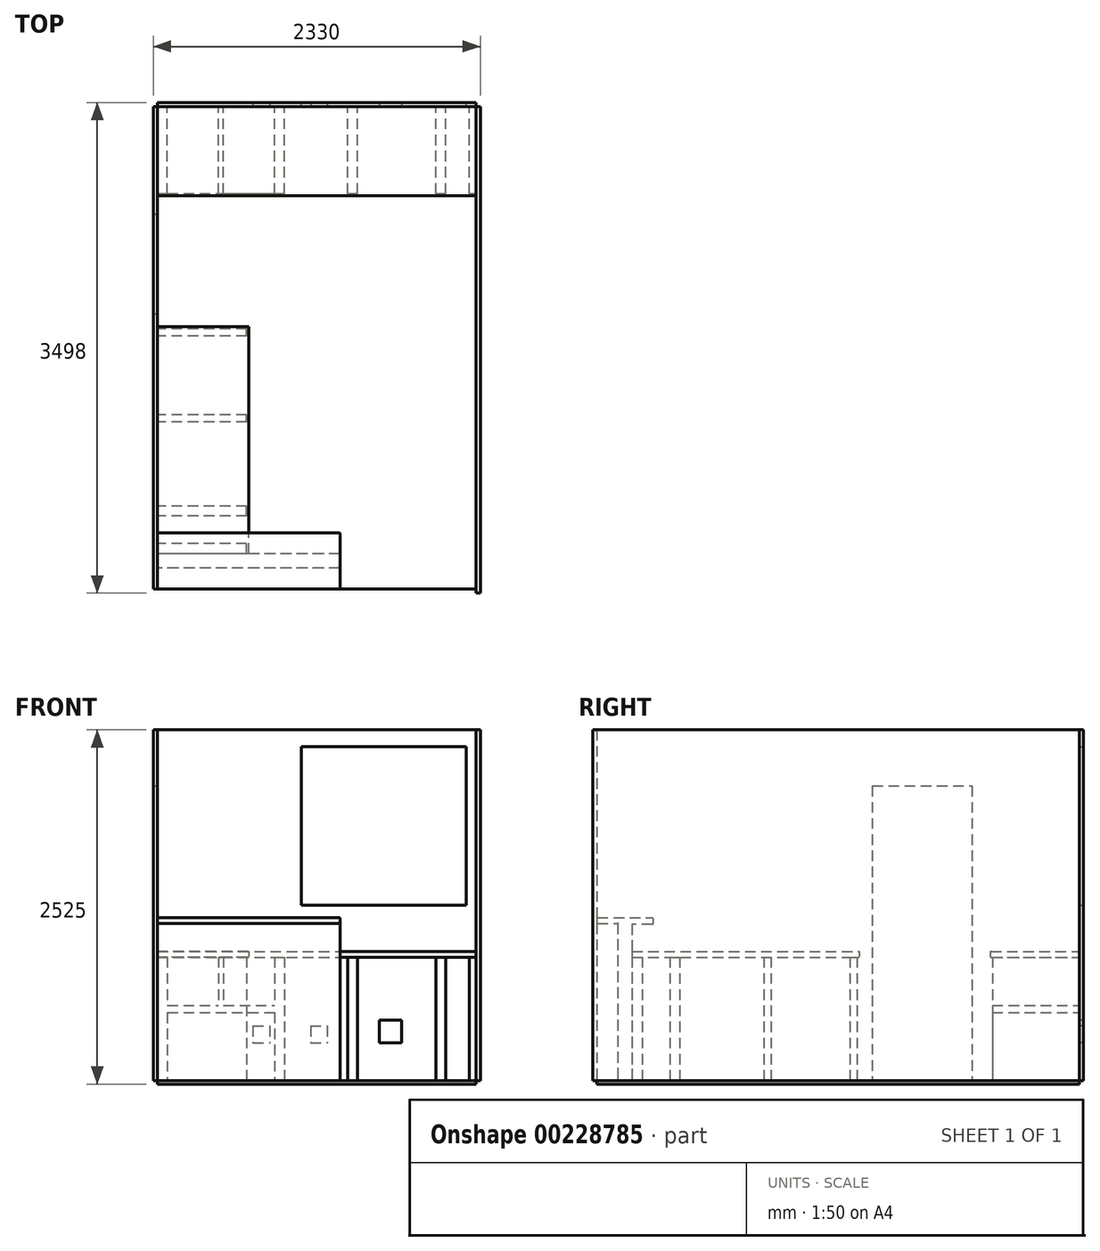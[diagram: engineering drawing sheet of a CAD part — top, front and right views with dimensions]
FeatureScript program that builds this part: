
annotation { "Feature Type Name" : "Feature", "Feature Type Description" : "" }
export const myFeature = defineFeature(function(context is Context, id is Id, definition is map)
    precondition{}
    {
        {
            var Q0;
            Q0=qCreatedBy(makeId("Top.planeOp"),FACE);
            var sketch = newSketch(context, id + "F0", { "sketchPlane" : qUnion([Q0])});
            skLineSegment(sketch, "E0.bottom", {"start": v(-166.7, 1726.55) * mm, "end": v(-136.7, 1726.55) * mm});
            skLineSegment(sketch, "E0.top", {"start": v(-166.7, -1711.45) * mm, "end": v(-136.7, -1711.45) * mm});
            skLineSegment(sketch, "E0.left", {"start": v(-166.7, 1726.55) * mm, "end": v(-166.7, -1711.45) * mm});
            skLineSegment(sketch, "E0.right", {"start": v(-136.7, 1726.55) * mm, "end": v(-136.7, -1711.45) * mm});
            skLineSegment(sketch, "E1.bottom", {"start": v(-136.7, 1756.55) * mm, "end": v(2133.3, 1756.55) * mm});
            skLineSegment(sketch, "E1.top", {"start": v(-136.7, 1726.55) * mm, "end": v(2133.3, 1726.55) * mm});
            skLineSegment(sketch, "E1.left", {"start": v(-136.7, 1756.55) * mm, "end": v(-136.7, 1726.55) * mm});
            skLineSegment(sketch, "E1.right", {"start": v(2133.3, 1756.55) * mm, "end": v(2133.3, 1726.55) * mm});
            skLineSegment(sketch, "E2.bottom", {"start": v(2133.3, 1726.55) * mm, "end": v(2163.3, 1726.55) * mm});
            skLineSegment(sketch, "E2.top", {"start": v(2133.3, -1741.45) * mm, "end": v(2163.3, -1741.45) * mm});
            skLineSegment(sketch, "E2.left", {"start": v(2133.3, 1726.55) * mm, "end": v(2133.3, -1741.45) * mm});
            skLineSegment(sketch, "E2.right", {"start": v(2163.3, 1726.55) * mm, "end": v(2163.3, -1741.45) * mm});
            skLineSegment(sketch, "E3.bottom", {"start": v(-166.7, 961.55) * mm, "end": v(-136.7, 961.55) * mm});
            skLineSegment(sketch, "E3.top", {"start": v(-166.7, 251.55) * mm, "end": v(-136.7, 251.55) * mm});
            skLineSegment(sketch, "E3.left", {"start": v(-166.7, 961.55) * mm, "end": v(-166.7, 251.55) * mm});
            skLineSegment(sketch, "E3.right", {"start": v(-136.7, 961.55) * mm, "end": v(-136.7, 251.55) * mm});
            skSolve(sketch);
        }
        {
            var Q0;
            Q0=makeQuery(id+"F0.imprint","IMPRINT",FACE,{"disambiguationData":[TD([[makeQuery(id+"F0.imprint","IMPRINT",EDGE,{"derivedFrom":sQuery(id+"F0.wireOp",EDGE,"E1.bottom")}),-1.0]])]});
            var Q1;
            Q1=makeQuery(id+"F0.imprint","IMPRINT",FACE,{"disambiguationData":[TD([[makeQuery(id+"F0.imprint","IMPRINT",EDGE,{"derivedFrom":sQuery(id+"F0.wireOp",EDGE,"E2.bottom")}),-1.0]])]});
            var Q2;
            {var subQ0=sQuery(id+"F0.wireOp",EDGE,"E0.bottom");Q2=makeQuery(id+"F0.imprint","IMPRINT",FACE,{"disambiguationData":[TD([[makeQuery(id+"F0.imprint","IMPRINT",EDGE,{"derivedFrom":subQ0}),-1.0]])]});}
            var Q3;
            {var subQ0=sQuery(id+"F0.wireOp",EDGE,"E0.top");Q3=makeQuery(id+"F0.imprint","IMPRINT",FACE,{"disambiguationData":[TD([[makeQuery(id+"F0.imprint","IMPRINT",EDGE,{"derivedFrom":subQ0}),1.0]])]});}
            extrude(context, id + "F1", {"entities" : qUnion([Q0, Q1, Q2, Q3]), "depth" : 2500 * mm});
        }
        {
            var Q0;
            Q0=makeQuery(id+"F1.opExtrude","CAP_FACE",FACE,{"disambiguationData":[OSD([sQuery(id+"F0.wireOp",EDGE,"E0.top"),sQuery(id+"F0.wireOp",EDGE,"E0.left"),sQuery(id+"F0.wireOp",EDGE,"E0.right"),sQuery(id+"F0.wireOp",EDGE,"E3.top")])],"isStart":true});
            var sketch = newSketch(context, id + "F2", { "sketchPlane" : qUnion([Q0])});
            skLineSegment(sketch, "E4.bottom", {"start": v(-136.7, 1711.45) * mm, "end": v(2133.3, 1711.45) * mm});
            skLineSegment(sketch, "E4.top", {"start": v(-136.7, -1726.55) * mm, "end": v(2133.3, -1726.55) * mm});
            skLineSegment(sketch, "E4.left", {"start": v(-136.7, 1711.45) * mm, "end": v(-136.7, -1726.55) * mm});
            skLineSegment(sketch, "E4.right", {"start": v(2133.3, 1711.45) * mm, "end": v(2133.3, -1726.55) * mm});
            skSolve(sketch);
        }
        {
            var Q0;
            Q0 = qSketchRegion(id + "F2", true);
            extrude(context, id + "F3", {"entities" : qUnion([Q0]), "depth" : 25 * mm});
        }
        {
            var Q0;
            Q0=makeQuery(id+"F1.opExtrude","SWEPT_FACE",FACE,{"disambiguationData":[OSD([sQuery(id+"F0.wireOp",EDGE,"E1.top")])]});
            var sketch = newSketch(context, id + "F4", { "sketchPlane" : qUnion([Q0])});
            skLineSegment(sketch, "E5.bottom", {"start": v(-136.7, 2500) * mm, "end": v(2133.3, 2500) * mm, "construction": true});
            skLineSegment(sketch, "E5.top", {"start": v(-136.7, 0) * mm, "end": v(2133.3, 0) * mm, "construction": true});
            skLineSegment(sketch, "E5.left", {"start": v(-136.7, 2500) * mm, "end": v(-136.7, 0) * mm, "construction": true});
            skLineSegment(sketch, "E5.right", {"start": v(2133.3, 2500) * mm, "end": v(2133.3, 0) * mm, "construction": true});
            skLineSegment(sketch, "E6", {"start": v(-136.7, 920) * mm, "end": v(2133.3, 920) * mm, "construction": true});
            skLineSegment(sketch, "E7.bottom", {"start": v(-136.7, 920) * mm, "end": v(2133.3, 920) * mm});
            skLineSegment(sketch, "E7.top", {"start": v(-136.7, 880) * mm, "end": v(2133.3, 880) * mm});
            skLineSegment(sketch, "E7.left", {"start": v(-136.7, 920) * mm, "end": v(-136.7, 880) * mm});
            skLineSegment(sketch, "E7.right", {"start": v(2133.3, 920) * mm, "end": v(2133.3, 880) * mm});
            skLineSegment(sketch, "E8.bottom", {"start": v(543.3, 390) * mm, "end": v(663.3, 390) * mm});
            skLineSegment(sketch, "E8.top", {"start": v(543.3, 270) * mm, "end": v(663.3, 270) * mm});
            skLineSegment(sketch, "E8.left", {"start": v(543.3, 390) * mm, "end": v(543.3, 270) * mm});
            skLineSegment(sketch, "E8.right", {"start": v(663.3, 390) * mm, "end": v(663.3, 270) * mm});
            skLineSegment(sketch, "E9.bottom", {"start": v(953.3, 390) * mm, "end": v(1073.3, 390) * mm});
            skLineSegment(sketch, "E9.top", {"start": v(953.3, 270) * mm, "end": v(1073.3, 270) * mm});
            skLineSegment(sketch, "E9.left", {"start": v(953.3, 390) * mm, "end": v(953.3, 270) * mm});
            skLineSegment(sketch, "E9.right", {"start": v(1073.3, 390) * mm, "end": v(1073.3, 270) * mm});
            skLineSegment(sketch, "E10.bottom", {"start": v(1443.3, 430) * mm, "end": v(1603.3, 430) * mm});
            skLineSegment(sketch, "E10.top", {"start": v(1443.3, 270) * mm, "end": v(1603.3, 270) * mm});
            skLineSegment(sketch, "E10.left", {"start": v(1443.3, 430) * mm, "end": v(1443.3, 270) * mm});
            skLineSegment(sketch, "E10.right", {"start": v(1603.3, 430) * mm, "end": v(1603.3, 270) * mm});
            skSolve(sketch);
        }
        {
            var Q0;
            Q0=makeQuery(id+"F4.imprint","IMPRINT",FACE,{"disambiguationData":[TD([[makeQuery(id+"F4.imprint","IMPRINT",EDGE,{"derivedFrom":sQuery(id+"F4.wireOp",EDGE,"E7.bottom")}),-1.0]])]});
            extrude(context, id + "F5", {"entities" : qUnion([Q0]), "depth" : 635 * mm});
        }
        {
            var Q0;
            {var subQ0=sQuery(id+"F0.wireOp",EDGE,"E0.right");Q0=makeQuery(id+"F1.opExtrude","SWEPT_FACE",FACE,{"disambiguationData":[OSD([subQ0]),TDD([makeQuery(id+"F0.imprint","IMPRINT",EDGE,{"disambiguationData":[TD([[makeQuery(id+"F0.imprint","INTERSECT",VERTEX,{"derivedFrom":[sQuery(id+"F0.wireOp",EDGE,"E0.top"),subQ0]}),1.0]])],"derivedFrom":subQ0})])]});}
            var sketch = newSketch(context, id + "F6", { "sketchPlane" : qUnion([Q0])});
            skLineSegment(sketch, "E11.top", {"start": v(-1461.45, 880) * mm, "end": v(159.45, 880) * mm});
            skLineSegment(sketch, "E11.left", {"start": v(-1461.45, 920) * mm, "end": v(-1461.45, 880) * mm});
            skLineSegment(sketch, "E11.right", {"start": v(159.45, 920) * mm, "end": v(159.45, 880) * mm});
            skLineSegment(sketch, "E12", {"start": v(-1511.45, 1160) * mm, "end": v(-1711.45, 1160) * mm});
            skLineSegment(sketch, "E13", {"start": v(-1711.45, 1120) * mm, "end": v(-1561.45, 1120) * mm});
            skLineSegment(sketch, "E14", {"start": v(-1561.45, 1120) * mm, "end": v(-1561.45, 0) * mm});
            skLineSegment(sketch, "E15.MirrorCS", {"start": v(-1311.45, 1113.32) * mm, "end": v(-1460.49, 1113.32) * mm});
            skLineSegment(sketch, "E16.MirrorCS", {"start": v(-1511.45, 1160) * mm, "end": v(-1311.45, 1160) * mm});
            skLineSegment(sketch, "E17", {"start": v(-1711.45, 1160) * mm, "end": v(-1711.45, 1120) * mm});
            skLineSegment(sketch, "E18", {"start": v(-1311.45, 1160) * mm, "end": v(-1311.45, 1113.32) * mm});
            skLineSegment(sketch, "E19", {"start": v(-1561.45, 0) * mm, "end": v(-1461.45, 0) * mm});
            skLineSegment(sketch, "E20", {"start": v(-1460.55, 920) * mm, "end": v(-1460.55, 880) * mm});
            skLineSegment(sketch, "E21", {"start": v(-1460.55, 920) * mm, "end": v(159.45, 920) * mm});
            skLineSegment(sketch, "E22", {"start": v(-1460.49, 1113.32) * mm, "end": v(-1461.45, 0) * mm});
            skSolve(sketch);
        }
        {
            var Q0;
            Q0=makeQuery(id+"F6.imprint","IMPRINT",FACE,{"disambiguationData":[TD([[makeQuery(id+"F6.imprint","IMPRINT",EDGE,{"derivedFrom":sQuery(id+"F6.wireOp",EDGE,"E12")}),1.0]])]});
            extrude(context, id + "F7", {"entities" : qUnion([Q0]), "depth" : 1300 * mm});
        }
        {
            var Q0;
            {var subQ0=sQuery(id+"F6.wireOp",EDGE,"E11.right");Q0=makeQuery(id+"F6.imprint","IMPRINT",FACE,{"disambiguationData":[TD([[makeQuery(id+"F6.imprint","IMPRINT",EDGE,{"derivedFrom":subQ0}),-1.0]])]});}
            extrude(context, id + "F8", {"entities" : qUnion([Q0]), "operationType" : NewBodyOperationType.ADD, "depth" : 650 * mm});
        }
        {
            var Q0;
            Q0=makeQuery(id+"F1.opExtrude","SWEPT_FACE",FACE,{"disambiguationData":[OSD([sQuery(id+"F0.wireOp",EDGE,"E1.bottom")])]});
            var sketch = newSketch(context, id + "F9", { "sketchPlane" : qUnion([Q0])});
            skLineSegment(sketch, "E23.bottom", {"start": v(-886.3, 2380) * mm, "end": v(-2063.3, 2380) * mm});
            skLineSegment(sketch, "E23.top", {"start": v(-886.3, 1250) * mm, "end": v(-2063.3, 1250) * mm});
            skLineSegment(sketch, "E23.left", {"start": v(-886.3, 2380) * mm, "end": v(-886.3, 1250) * mm});
            skLineSegment(sketch, "E23.right", {"start": v(-2063.3, 2380) * mm, "end": v(-2063.3, 1250) * mm});
            skSolve(sketch);
        }
        {
            var Q0;
            Q0=makeQuery(id+"F9.imprint","IMPRINT",FACE,{"disambiguationData":[TD([[makeQuery(id+"F9.imprint","IMPRINT",EDGE,{"derivedFrom":sQuery(id+"F9.wireOp",EDGE,"E23.bottom")}),1.0]])]});
            extrude(context, id + "F10", {"entities" : qUnion([Q0]), "operationType" : NewBodyOperationType.REMOVE, "endBound" : BoundingType.THROUGH_ALL, "oppositeDirection" : true, "depth" : 25 * mm});
        }
        {
            var Q0;
            Q0=makeQuery(id+"F1.opExtrude","SWEPT_FACE",FACE,{"disambiguationData":[OSD([sQuery(id+"F0.wireOp",EDGE,"E3.bottom")])]});
            var sketch = newSketch(context, id + "F11", { "sketchPlane" : qUnion([Q0])});
            skLineSegment(sketch, "E24.bottom", {"start": v(-166.7, 2500) * mm, "end": v(-136.7, 2500) * mm});
            skLineSegment(sketch, "E24.top", {"start": v(-166.7, 2100) * mm, "end": v(-136.7, 2100) * mm});
            skLineSegment(sketch, "E24.left", {"start": v(-166.7, 2500) * mm, "end": v(-166.7, 2100) * mm});
            skLineSegment(sketch, "E24.right", {"start": v(-136.7, 2500) * mm, "end": v(-136.7, 2100) * mm});
            skSolve(sketch);
        }
        {
            var Q0;
            Q0=makeQuery(id+"F11.imprint","IMPRINT",FACE,{"disambiguationData":[TD([[makeQuery(id+"F11.imprint","IMPRINT",EDGE,{"derivedFrom":sQuery(id+"F11.wireOp",EDGE,"E24.bottom")}),-1.0]])]});
            extrude(context, id + "F12", {"entities" : qUnion([Q0]), "operationType" : NewBodyOperationType.ADD, "depth" : 710 * mm});
        }
        {
            var Q0;
            {var subQ0=sQuery(id+"F0.wireOp",EDGE,"E0.right");Q0=makeQuery(id+"F1.opExtrude","SWEPT_FACE",FACE,{"disambiguationData":[OSD([subQ0]),TDD([makeQuery(id+"F0.imprint","IMPRINT",EDGE,{"disambiguationData":[TD([[makeQuery(id+"F0.imprint","INTERSECT",VERTEX,{"derivedFrom":[sQuery(id+"F0.wireOp",EDGE,"E0.top"),subQ0]}),1.0]])],"derivedFrom":subQ0})])]});}
            var sketch = newSketch(context, id + "F13", { "sketchPlane" : qUnion([Q0])});
            skLineSegment(sketch, "E25", {"start": v(-1997.96, 880) * mm, "end": v(384.41, 880) * mm, "construction": true});
            skLineSegment(sketch, "E26", {"start": v(-1121.45, 0) * mm, "end": v(-1121.45, -0.15) * mm, "construction": true});
            skLineSegment(sketch, "E27.bottom", {"start": v(-1121.45, 880) * mm, "end": v(-1191.45, 880) * mm});
            skLineSegment(sketch, "E27.top", {"start": v(-1121.45, 0) * mm, "end": v(-1191.45, 0) * mm});
            skLineSegment(sketch, "E27.left", {"start": v(-1121.45, 880) * mm, "end": v(-1121.45, 0) * mm});
            skLineSegment(sketch, "E27.right", {"start": v(-1191.45, 880) * mm, "end": v(-1191.45, 0) * mm});
            skLineSegment(sketch, "E28.bottom", {"start": v(-1387.45, 880) * mm, "end": v(-1191.45, 880) * mm});
            skLineSegment(sketch, "E28.top", {"start": v(-1387.45, 0) * mm, "end": v(-1191.45, 0) * mm});
            skLineSegment(sketch, "E28.left", {"start": v(-1387.45, 880) * mm, "end": v(-1387.45, 0) * mm});
            skLineSegment(sketch, "E29.bottom", {"start": v(-1387.45, 880) * mm, "end": v(-1460.55, 880) * mm});
            skLineSegment(sketch, "E29.top", {"start": v(-1387.45, 0) * mm, "end": v(-1460.55, 0) * mm});
            skLineSegment(sketch, "E29.right", {"start": v(-1460.55, 880) * mm, "end": v(-1460.55, 0) * mm});
            skLineSegment(sketch, "E30.bottom", {"start": v(-1121.45, 880) * mm, "end": v(-521.45, 880) * mm});
            skLineSegment(sketch, "E30.top", {"start": v(-1121.45, 0) * mm, "end": v(-521.45, 0) * mm});
            skLineSegment(sketch, "E30.right", {"start": v(-521.45, 880) * mm, "end": v(-521.45, 0) * mm});
            skLineSegment(sketch, "E31.bottom", {"start": v(-521.45, 880) * mm, "end": v(-471.45, 880) * mm});
            skLineSegment(sketch, "E31.top", {"start": v(-521.45, 0) * mm, "end": v(-471.45, 0) * mm});
            skLineSegment(sketch, "E31.right", {"start": v(-471.45, 880) * mm, "end": v(-471.45, 0) * mm});
            skLineSegment(sketch, "E32.bottom", {"start": v(-471.45, 880) * mm, "end": v(92.55, 880) * mm});
            skLineSegment(sketch, "E32.top", {"start": v(-471.45, 0) * mm, "end": v(92.55, 0) * mm});
            skLineSegment(sketch, "E32.right", {"start": v(92.55, 880) * mm, "end": v(92.55, 0) * mm});
            skLineSegment(sketch, "E33.bottom", {"start": v(92.55, 880) * mm, "end": v(142.55, 880) * mm});
            skLineSegment(sketch, "E33.top", {"start": v(92.55, 0) * mm, "end": v(142.55, 0) * mm});
            skLineSegment(sketch, "E33.right", {"start": v(142.55, 880) * mm, "end": v(142.55, 0) * mm});
            skLineSegment(sketch, "E34", {"start": v(-821.45, 2500) * mm, "end": v(-821.45, 0) * mm, "construction": true});
            skSolve(sketch);
        }
        {
            var Q0;
            Q0=makeQuery(id+"F13.imprint","IMPRINT",FACE,{"disambiguationData":[TD([[makeQuery(id+"F13.imprint","IMPRINT",EDGE,{"derivedFrom":sQuery(id+"F13.wireOp",EDGE,"E27.bottom")}),-1.0]])]});
            var Q1;
            Q1=makeQuery(id+"F13.imprint","IMPRINT",FACE,{"disambiguationData":[TD([[makeQuery(id+"F13.imprint","IMPRINT",EDGE,{"derivedFrom":sQuery(id+"F13.wireOp",EDGE,"E29.bottom")}),-1.0]])]});
            var Q2;
            Q2=makeQuery(id+"F13.imprint","IMPRINT",FACE,{"disambiguationData":[TD([[makeQuery(id+"F13.imprint","IMPRINT",EDGE,{"derivedFrom":sQuery(id+"F13.wireOp",EDGE,"E31.bottom")}),-1.0]])]});
            var Q3;
            Q3=makeQuery(id+"F13.imprint","IMPRINT",FACE,{"disambiguationData":[TD([[makeQuery(id+"F13.imprint","IMPRINT",EDGE,{"derivedFrom":sQuery(id+"F13.wireOp",EDGE,"E33.bottom")}),-1.0]])]});
            extrude(context, id + "F14", {"entities" : qUnion([Q0, Q1, Q2, Q3]), "depth" : 635 * mm});
        }
        {
            var Q0;
            Q0=makeQuery(id+"F8.opExtrude","SWEPT_EDGE",EDGE,{"disambiguationData":[OSD([sQuery(id+"F6.wireOp",EDGE,"E11.right"),sQuery(id+"F6.wireOp",EDGE,"E21")])]});
            var Q1;
            Q1=makeQuery(id+"F8.opExtrude","CAP_EDGE",EDGE,{"disambiguationData":[OSD([sQuery(id+"F6.wireOp",EDGE,"E21")])],"isStart":false});
            var Q2;
            Q2=makeQuery(id+"F8.opExtrude","SWEPT_EDGE",EDGE,{"disambiguationData":[OSD([sQuery(id+"F6.wireOp",EDGE,"E11.top"),sQuery(id+"F6.wireOp",EDGE,"E11.right")])]});
            var Q3;
            Q3=makeQuery(id+"F8.opExtrude","CAP_EDGE",EDGE,{"disambiguationData":[OSD([sQuery(id+"F6.wireOp",EDGE,"E11.top")])],"isStart":false});
            fillet(context, id + "F15", {"entities" : qUnion([Q0, Q1, Q2, Q3]), "radius" : 5 * mm, "tangentPropagation" : true, "allowEdgeOverflow" : false});
        }
        {
            var Q0;
            Q0=makeQuery(id+"F7.opExtrude","SWEPT_EDGE",EDGE,{"disambiguationData":[OSD([sQuery(id+"F0.wireOp",EDGE,"E0.top"),sQuery(id+"F0.wireOp",EDGE,"E0.right"),sQuery(id+"F6.wireOp",EDGE,"E12"),sQuery(id+"F6.wireOp",EDGE,"E17")])]});
            var Q1;
            Q1=makeQuery(id+"F7.opExtrude","SWEPT_EDGE",EDGE,{"disambiguationData":[OSD([sQuery(id+"F6.wireOp",EDGE,"E16.MirrorCS"),sQuery(id+"F6.wireOp",EDGE,"E18")])]});
            var Q2;
            Q2=makeQuery(id+"F7.opExtrude","CAP_EDGE",EDGE,{"disambiguationData":[OSD([sQuery(id+"F6.wireOp",EDGE,"E12"),sQuery(id+"F6.wireOp",EDGE,"E16.MirrorCS")])],"isStart":false});
            var Q3;
            Q3=makeQuery(id+"F7.opExtrude","SWEPT_EDGE",EDGE,{"disambiguationData":[OSD([sQuery(id+"F0.wireOp",EDGE,"E0.top"),sQuery(id+"F0.wireOp",EDGE,"E0.right"),sQuery(id+"F6.wireOp",EDGE,"E13"),sQuery(id+"F6.wireOp",EDGE,"E17")])]});
            var Q4;
            Q4=makeQuery(id+"F7.opExtrude","CAP_EDGE",EDGE,{"disambiguationData":[OSD([sQuery(id+"F6.wireOp",EDGE,"E13")])],"isStart":false});
            var Q5;
            Q5=makeQuery(id+"F7.opExtrude","CAP_EDGE",EDGE,{"disambiguationData":[OSD([sQuery(id+"F6.wireOp",EDGE,"E15.MirrorCS")])],"isStart":false});
            var Q6;
            Q6=makeQuery(id+"F7.opExtrude","CAP_EDGE",EDGE,{"disambiguationData":[OSD([sQuery(id+"F6.wireOp",EDGE,"E17")])],"isStart":false});
            var Q7;
            Q7=makeQuery(id+"F7.opExtrude","CAP_EDGE",EDGE,{"disambiguationData":[OSD([sQuery(id+"F6.wireOp",EDGE,"E18")])],"isStart":false});
            var Q8;
            Q8=makeQuery(id+"F7.opExtrude","SWEPT_EDGE",EDGE,{"disambiguationData":[OSD([sQuery(id+"F6.wireOp",EDGE,"E15.MirrorCS"),sQuery(id+"F6.wireOp",EDGE,"E18")])]});
            fillet(context, id + "F16", {"entities" : qUnion([Q0, Q1, Q2, Q3, Q4, Q5, Q6, Q7, Q8]), "radius" : 5 * mm, "tangentPropagation" : true, "allowEdgeOverflow" : false});
        }
        {
            var Q0;
            Q0=makeQuery(id+"F5.opExtrude","CAP_EDGE",EDGE,{"disambiguationData":[OSD([sQuery(id+"F4.wireOp",EDGE,"E7.bottom")])],"isStart":false});
            var Q1;
            Q1=makeQuery(id+"F5.opExtrude","CAP_EDGE",EDGE,{"disambiguationData":[OSD([sQuery(id+"F4.wireOp",EDGE,"E7.top")])],"isStart":false});
            fillet(context, id + "F17", {"entities" : qUnion([Q0, Q1]), "radius" : 5 * mm, "tangentPropagation" : true, "allowEdgeOverflow" : false});
        }
        {
            var Q0;
            {var subQ0=sQuery(id+"F4.wireOp",EDGE,"E7.top");Q0=makeQuery(id+"F4.imprint","IMPRINT",FACE,{"disambiguationData":[TD([[makeQuery(id+"F4.imprint","IMPRINT",EDGE,{"derivedFrom":subQ0}),-1.0]])]});}
            var sketch = newSketch(context, id + "F18", { "sketchPlane" : qUnion([Q0])});
            skLineSegment(sketch, "E35", {"start": v(-136.7, 0) * mm, "end": v(-136.7, 880) * mm, "construction": true});
            skLineSegment(sketch, "E36", {"start": v(2133.3, 0) * mm, "end": v(2133.3, 880) * mm, "construction": true});
            skLineSegment(sketch, "E37", {"start": v(-136.7, 880) * mm, "end": v(2133.3, 880) * mm, "construction": true});
            skLineSegment(sketch, "E38.bottom", {"start": v(2133.3, 880) * mm, "end": v(2083.3, 880) * mm});
            skLineSegment(sketch, "E38.top", {"start": v(2133.3, 0) * mm, "end": v(2083.3, 0) * mm});
            skLineSegment(sketch, "E38.left", {"start": v(2133.3, 880) * mm, "end": v(2133.3, 0) * mm});
            skLineSegment(sketch, "E38.right", {"start": v(2083.3, 880) * mm, "end": v(2083.3, 0) * mm});
            skLineSegment(sketch, "E39.bottom", {"start": v(1287.3, 880) * mm, "end": v(1217.3, 880) * mm});
            skLineSegment(sketch, "E39.top", {"start": v(1287.3, 0) * mm, "end": v(1217.3, 0) * mm});
            skLineSegment(sketch, "E39.left", {"start": v(1287.3, 880) * mm, "end": v(1287.3, 0) * mm});
            skLineSegment(sketch, "E39.right", {"start": v(1217.3, 880) * mm, "end": v(1217.3, 0) * mm});
            skLineSegment(sketch, "E40.bottom", {"start": v(697.3, 880) * mm, "end": v(767.3, 880) * mm});
            skLineSegment(sketch, "E40.top", {"start": v(697.3, 0) * mm, "end": v(767.3, 0) * mm});
            skLineSegment(sketch, "E40.left", {"start": v(697.3, 880) * mm, "end": v(697.3, 0) * mm});
            skLineSegment(sketch, "E40.right", {"start": v(767.3, 880) * mm, "end": v(767.3, 0) * mm});
            skLineSegment(sketch, "E41.bottom", {"start": v(-136.7, 880) * mm, "end": v(-66.7, 880) * mm});
            skLineSegment(sketch, "E41.top", {"start": v(-136.7, 0) * mm, "end": v(-66.7, 0) * mm});
            skLineSegment(sketch, "E41.left", {"start": v(-136.7, 880) * mm, "end": v(-136.7, 0) * mm});
            skLineSegment(sketch, "E41.right", {"start": v(-66.7, 880) * mm, "end": v(-66.7, 0) * mm});
            skLineSegment(sketch, "E42.bottom", {"start": v(297.3, 880) * mm, "end": v(333.3, 880) * mm});
            skLineSegment(sketch, "E42.top", {"start": v(297.3, 535) * mm, "end": v(333.3, 535) * mm});
            skLineSegment(sketch, "E42.left", {"start": v(297.3, 880) * mm, "end": v(297.3, 535) * mm});
            skLineSegment(sketch, "E42.right", {"start": v(333.3, 880) * mm, "end": v(333.3, 535) * mm});
            skLineSegment(sketch, "E43.left", {"start": v(-66.7, 535) * mm, "end": v(-66.7, 470) * mm});
            skLineSegment(sketch, "E44.bottom", {"start": v(-66.7, 535) * mm, "end": v(697.3, 535) * mm});
            skLineSegment(sketch, "E44.top", {"start": v(-66.7, 485) * mm, "end": v(697.3, 485) * mm});
            skLineSegment(sketch, "E44.left", {"start": v(-66.7, 535) * mm, "end": v(-66.7, 485) * mm});
            skLineSegment(sketch, "E44.right", {"start": v(697.3, 535) * mm, "end": v(697.3, 485) * mm});
            skLineSegment(sketch, "E45.bottom", {"start": v(1847.3, 880) * mm, "end": v(1917.3, 880) * mm});
            skLineSegment(sketch, "E45.top", {"start": v(1847.3, 0) * mm, "end": v(1917.3, 0) * mm});
            skLineSegment(sketch, "E45.left", {"start": v(1847.3, 880) * mm, "end": v(1847.3, 0) * mm});
            skLineSegment(sketch, "E45.right", {"start": v(1917.3, 880) * mm, "end": v(1917.3, 0) * mm});
            skSolve(sketch);
        }
        {
            var Q0;
            Q0 = qSketchRegion(id + "F18", true);
            extrude(context, id + "F19", {"entities" : qUnion([Q0]), "depth" : 620 * mm});
        }
        {
            var Q0;
            Q0=makeQuery(id+"F4.imprint","IMPRINT",FACE,{"disambiguationData":[TD([[makeQuery(id+"F4.imprint","IMPRINT",EDGE,{"derivedFrom":sQuery(id+"F4.wireOp",EDGE,"E10.bottom")}),-1.0]])]});
            var Q1;
            Q1=makeQuery(id+"F4.imprint","IMPRINT",FACE,{"disambiguationData":[TD([[makeQuery(id+"F4.imprint","IMPRINT",EDGE,{"derivedFrom":sQuery(id+"F4.wireOp",EDGE,"E9.bottom")}),-1.0]])]});
            var Q2;
            Q2=makeQuery(id+"F4.imprint","IMPRINT",FACE,{"disambiguationData":[TD([[makeQuery(id+"F4.imprint","IMPRINT",EDGE,{"derivedFrom":sQuery(id+"F4.wireOp",EDGE,"E8.bottom")}),-1.0]])]});
            extrude(context, id + "F20", {"entities" : qUnion([Q0, Q1, Q2]), "operationType" : NewBodyOperationType.REMOVE, "oppositeDirection" : true, "depth" : 25 * mm});
        }
    });
